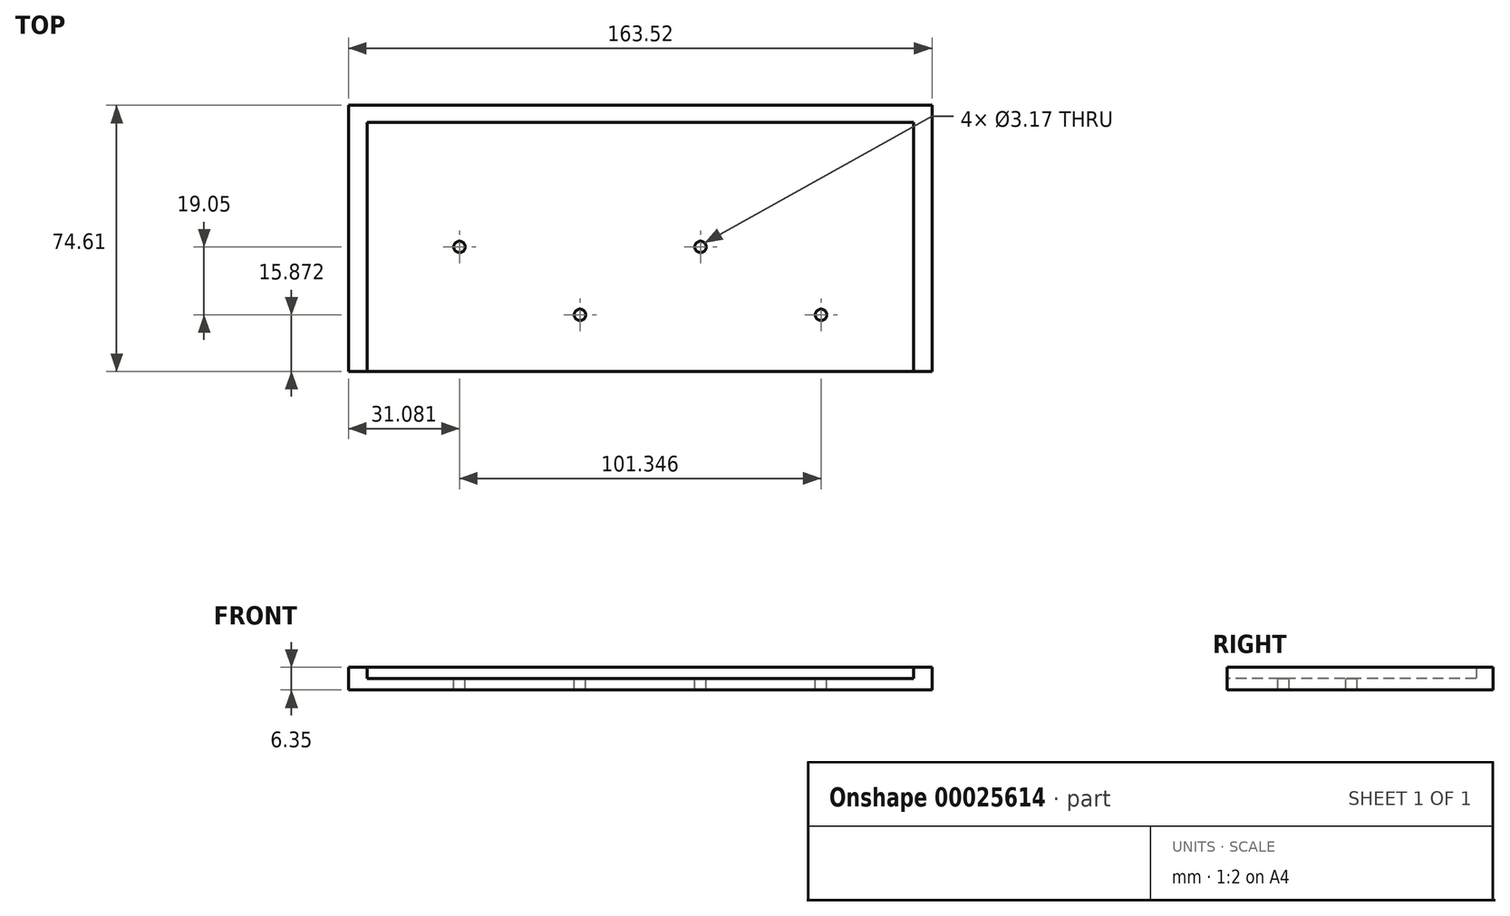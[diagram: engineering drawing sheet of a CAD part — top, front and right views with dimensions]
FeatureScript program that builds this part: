
annotation { "Feature Type Name" : "Feature", "Feature Type Description" : "" }
export const myFeature = defineFeature(function(context is Context, id is Id, definition is map)
    precondition{}
    {
        {
            var Q0;
            Q0=qCreatedBy(makeId("Top.planeOp"),FACE);
            var sketch = newSketch(context, id + "F0", { "sketchPlane" : qUnion([Q0])});
            skLineSegment(sketch, "E0.rect.bottom", {"start": v(77, -36.51) * mm, "end": v(-77, -36.51) * mm});
            skPoint(sketch, "E0.rect.middle", {"position": v(0, 0) * mm});
            skCircle(sketch, "E1", {"center": v(-50.68, -1.59) * mm, "radius": 1.59 * mm});
            skCircle(sketch, "E2", {"center": v(-16.9, -20.64) * mm, "radius": 1.59 * mm});
            skCircle(sketch, "E3", {"center": v(16.88, -1.59) * mm, "radius": 1.59 * mm});
            skCircle(sketch, "E4", {"center": v(50.67, -20.64) * mm, "radius": 1.59 * mm});
            skLineSegment(sketch, "E5", {"start": v(-77, -36.51) * mm, "end": v(-81.76, -36.51) * mm});
            skLineSegment(sketch, "E6", {"start": v(-81.76, -36.51) * mm, "end": v(-81.76, 28.57) * mm});
            skLineSegment(sketch, "E7", {"start": v(81.76, 28.58) * mm, "end": v(81.76, -36.51) * mm});
            skLineSegment(sketch, "E8", {"start": v(81.76, -36.51) * mm, "end": v(77, -36.51) * mm});
            skPoint(sketch, "E0.rect.top.end.orphan", {"position": v(-77, 36.51) * mm});
            skPoint(sketch, "E9.orphan", {"position": v(77, 36.51) * mm});
            skLineSegment(sketch, "E10", {"start": v(-76.6, 23.81) * mm, "end": v(-76.6, -36.51) * mm});
            skLineSegment(sketch, "E11", {"start": v(76.6, 23.81) * mm, "end": v(76.6, -36.51) * mm});
            skLineSegment(sketch, "E12", {"start": v(-76.6, 23.81) * mm, "end": v(-76.6, 33.34) * mm});
            skLineSegment(sketch, "E13", {"start": v(-76.6, 33.34) * mm, "end": v(76.6, 33.34) * mm});
            skLineSegment(sketch, "E14", {"start": v(76.6, 33.34) * mm, "end": v(76.6, 23.81) * mm});
            skLineSegment(sketch, "E15", {"start": v(-81.76, 28.57) * mm, "end": v(-81.76, 38.1) * mm});
            skLineSegment(sketch, "E16", {"start": v(-81.76, 38.1) * mm, "end": v(81.76, 38.1) * mm});
            skLineSegment(sketch, "E17", {"start": v(81.76, 38.1) * mm, "end": v(81.76, 28.58) * mm});
            skSolve(sketch);
        }
        {
            var Q0;
            Q0 = qSketchRegion(id + "F0", true);
            extrude(context, id + "F1", {"entities" : qUnion([Q0]), "oppositeDirection" : true, "depth" : 3.17 * mm});
        }
        {
            var Q0;
            {var subQ4=sQuery(id+"F0.wireOp",EDGE,"E5");Q0=makeQuery(id+"F0.imprint","IMPRINT",FACE,{"disambiguationData":[TD([[makeQuery(id+"F0.imprint","IMPRINT",EDGE,{"derivedFrom":subQ4}),-1.0]])]});}
            extrude(context, id + "F2", {"entities" : qUnion([Q0]), "operationType" : NewBodyOperationType.ADD, "depth" : 3.17 * mm});
        }
    });
